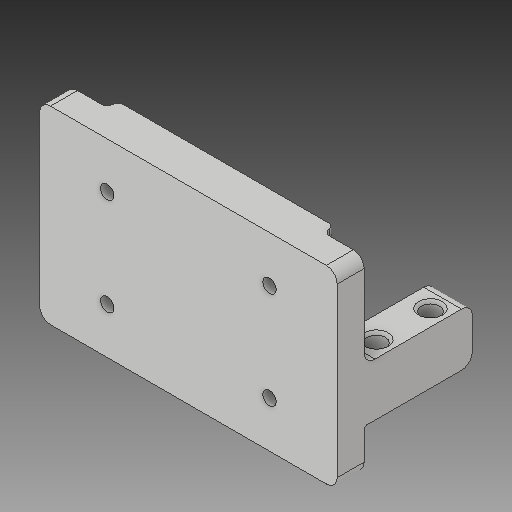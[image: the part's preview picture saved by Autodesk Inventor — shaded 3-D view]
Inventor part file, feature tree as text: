
AUTODESK INVENTOR PART (.ipt)
format: ipt  version: 2019 (Build 230136000, 136)  size: 172,544 bytes
history: native  units: mm
features: sketch x4, other x3
ambient origin geometry x8: Origin, YZ Plane, XZ Plane, XY Plane, X Axis, Y Axis, Z Axis, Center Point
bodies: Solid1 (feature_tree)
feature tree (7):
  other  "big_servo_hold.ipt"
  other  "Solid1::big_servo_hold.ipt"
  other  "TaggingFeature1"
  sketch  "Sketch1"  dims[d0=10.0mm]
  sketch  "Sketch2"
  sketch  "Sketch3"
  sketch  "Sketch4"
